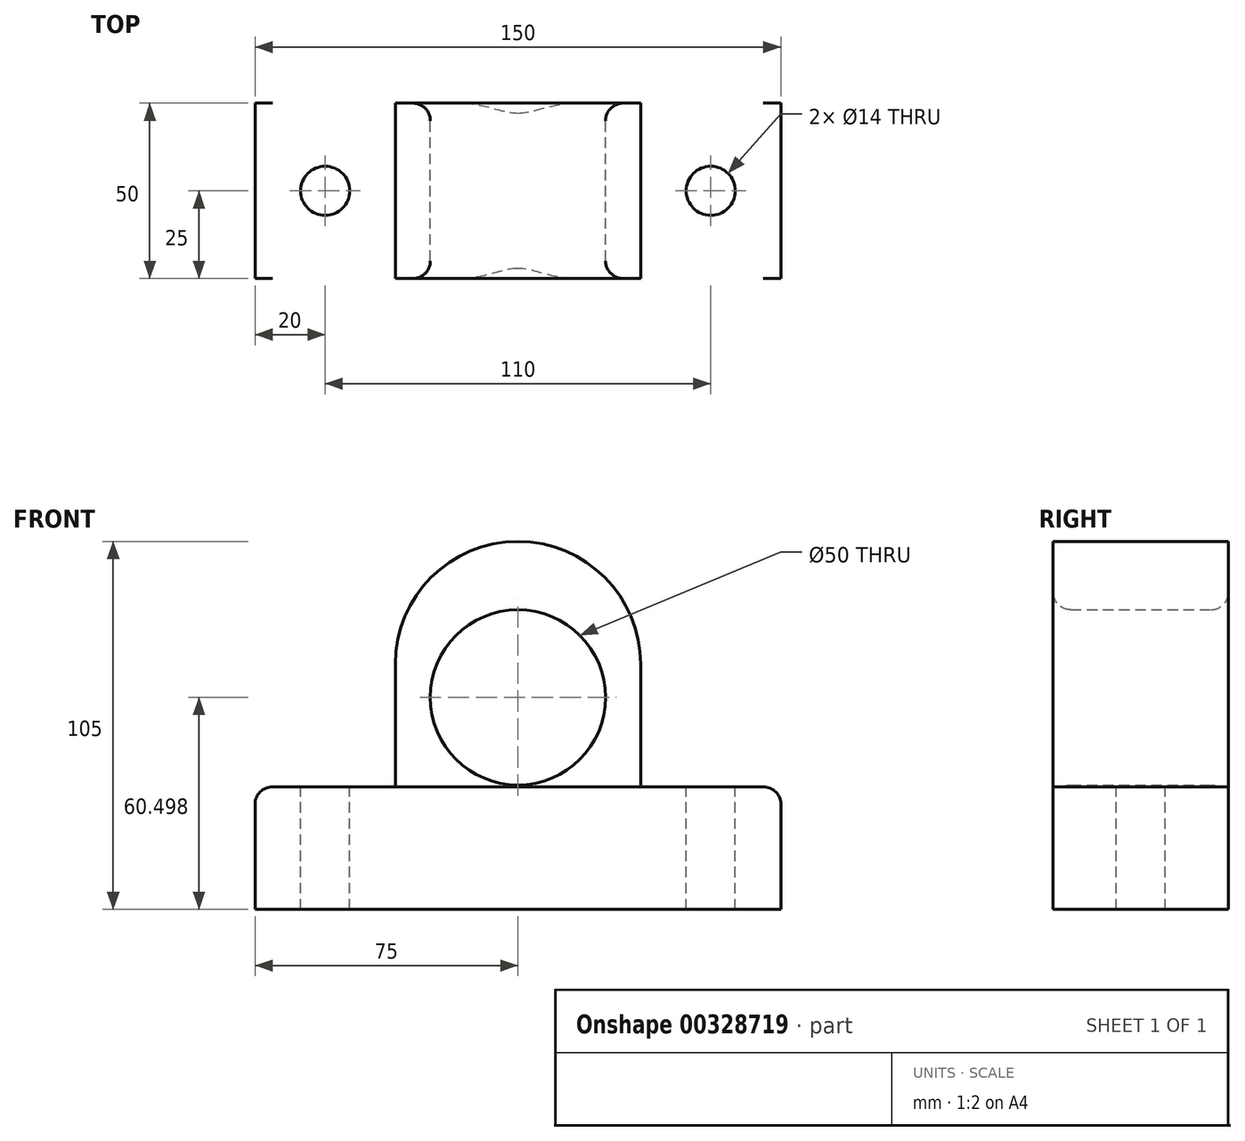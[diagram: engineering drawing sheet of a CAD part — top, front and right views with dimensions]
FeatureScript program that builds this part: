
annotation { "Feature Type Name" : "Feature", "Feature Type Description" : "" }
export const myFeature = defineFeature(function(context is Context, id is Id, definition is map)
    precondition{}
    {
        {
            var Q0;
            Q0=qCreatedBy(makeId("Front.planeOp"),FACE);
            var sketch = newSketch(context, id + "F0", { "sketchPlane" : qUnion([Q0])});
            skLineSegment(sketch, "E0.bottom", {"start": v(75, -17.5) * mm, "end": v(-75, -17.5) * mm});
            skLineSegment(sketch, "E0.top", {"start": v(75, 17.5) * mm, "end": v(-75, 17.5) * mm});
            skLineSegment(sketch, "E0.left", {"start": v(75, -17.5) * mm, "end": v(75, 17.5) * mm});
            skLineSegment(sketch, "E0.right", {"start": v(-75, -17.5) * mm, "end": v(-75, 17.5) * mm});
            skPoint(sketch, "E0.middle", {"position": v(0, 0) * mm});
            skSolve(sketch);
        }
        {
            var Q0;
            Q0=qCreatedBy(makeId("Front.planeOp"),FACE);
            var sketch = newSketch(context, id + "F1", { "sketchPlane" : qUnion([Q0])});
            skLineSegment(sketch, "E1.bottom", {"start": v(-35, 17.5) * mm, "end": v(35, 17.5) * mm});
            skLineSegment(sketch, "E1.top", {"start": v(-35, 87.5) * mm, "end": v(35, 87.5) * mm});
            skLineSegment(sketch, "E1.left", {"start": v(-35, 17.5) * mm, "end": v(-35, 87.5) * mm});
            skLineSegment(sketch, "E1.right", {"start": v(35, 17.5) * mm, "end": v(35, 87.5) * mm});
            skCircle(sketch, "E2", {"center": v(0, 43) * mm, "radius": 25 * mm});
            skSolve(sketch);
        }
        {
            var Q0;
            Q0=makeQuery(id+"F0.imprint","IMPRINT",FACE,{"disambiguationData":[TD([[makeQuery(id+"F0.imprint","IMPRINT",EDGE,{"derivedFrom":sQuery(id+"F0.wireOp",EDGE,"E0.bottom")}),-1.0]])]});
            var Q1;
            Q1=makeQuery(id+"F1.imprint","IMPRINT",FACE,{"disambiguationData":[TD([[makeQuery(id+"F1.imprint","IMPRINT",EDGE,{"derivedFrom":sQuery(id+"F1.wireOp",EDGE,"E1.bottom")}),1.0]])]});
            extrude(context, id + "F2", {"entities" : qUnion([Q0, Q1]), "depth" : 50 * mm});
        }
        {
            var Q0;
            Q0=makeQuery(id+"F2.opExtrude","SWEPT_EDGE",EDGE,{"disambiguationData":[OSD([sQuery(id+"F1.wireOp",EDGE,"E1.top"),sQuery(id+"F1.wireOp",EDGE,"E1.right")])]});
            var Q1;
            Q1=makeQuery(id+"F2.opExtrude","SWEPT_EDGE",EDGE,{"disambiguationData":[OSD([sQuery(id+"F1.wireOp",EDGE,"E1.top"),sQuery(id+"F1.wireOp",EDGE,"E1.left")])]});
            fillet(context, id + "F3", {"entities" : qUnion([Q0, Q1]), "radius" : 35 * mm, "tangentPropagation" : true, "allowEdgeOverflow" : false});
        }
        {
            var Q0;
            Q0=makeQuery(id+"F2.opExtrude","CAP_EDGE",EDGE,{"disambiguationData":[OSD([sQuery(id+"F1.wireOp",EDGE,"E2")])],"isStart":true});
            var Q1;
            {var subQ0=sQuery(id+"F1.wireOp",EDGE,"E1.right");var subQ1=sQuery(id+"F1.wireOp",EDGE,"E1.top");Q1=makeQuery(id+"F3.opFillet","BLEND_EDGE",EDGE,{"blendedFrom":[makeQuery(id+"F2.opExtrude","SWEPT_EDGE",EDGE,{"disambiguationData":[OSD([subQ1,subQ0])]}),makeQuery(id+"F2.opExtrude","CAP_FACE",FACE,{"disambiguationData":[OSD([sQuery(id+"F1.wireOp",EDGE,"E1.bottom"),subQ1,sQuery(id+"F1.wireOp",EDGE,"E1.left"),subQ0,sQuery(id+"F1.wireOp",EDGE,"E2")])],"isStart":true})],"blendedInto":[makeQuery(id+"F2.opExtrude","CAP_FACE",FACE,{"disambiguationData":[OSD([sQuery(id+"F1.wireOp",EDGE,"E1.bottom"),subQ1,sQuery(id+"F1.wireOp",EDGE,"E1.left"),subQ0,sQuery(id+"F1.wireOp",EDGE,"E2")])],"isStart":true})]});}
            fillet(context, id + "F4", {"entities" : qUnion([Q0, Q1]), "radius" : 5 * mm, "tangentPropagation" : true, "allowEdgeOverflow" : false});
        }
        {
            var Q0;
            Q0=makeQuery(id+"F2.opExtrude","SWEPT_FACE",FACE,{"disambiguationData":[OSD([sQuery(id+"F0.wireOp",EDGE,"E0.top")])]});
            var sketch = newSketch(context, id + "F5", { "sketchPlane" : qUnion([Q0])});
            skCircle(sketch, "E3", {"center": v(-55, -25) * mm, "radius": 8 * mm});
            skCircle(sketch, "E4", {"center": v(55, -25) * mm, "radius": 8 * mm});
            skSolve(sketch);
        }
        {
            var Q0;
            Q0=sQuery(id+"F5.wireOp",VERTEX,"E3.center");
            var Q1;
            Q1=sQuery(id+"F5.wireOp",VERTEX,"E4.center");
            var Q2;
            Q2=makeQuery(id+"F2.opExtrude","SWEPT_BODY",BODY,{"disambiguationData":[OSD([sQuery(id+"F0.wireOp",EDGE,"E0.bottom"),sQuery(id+"F0.wireOp",EDGE,"E0.top"),sQuery(id+"F0.wireOp",EDGE,"E0.left"),sQuery(id+"F0.wireOp",EDGE,"E0.right")])]});
            hole(context, id + "F6", {"style" : HoleStyle.SIMPLE, "endStyle" : HoleEndStyle.THROUGH, "standardTappedOrClearance" : lookupTablePath({ "standard" : "ISO", "engagement" : "75%", "pitch" : "2 mm", "size" : "M16", "type" : "Tapped" }), "standardBlindInLast" : lookupTablePath({ "standard" : "ISO", "engagement" : "75%", "pitch" : "2 mm", "size" : "M16", "type" : "Tapped" }), "holeDiameter" : 14 * mm, "showTappedDepth" : true, "tappedDepth" : 12 * mm, "tapClearance" : 3, "locations" : qUnion([Q0, Q1]), "scope" : qUnion([Q2]), "majorDiameter" : 16 * mm});
        }
        {
            var Q0;
            Q0=makeQuery(id+"F2.opExtrude","CAP_EDGE",EDGE,{"disambiguationData":[OSD([sQuery(id+"F1.wireOp",EDGE,"E2")])],"isStart":false});
            var Q1;
            Q1=makeQuery(id+"F2.opExtrude","SWEPT_EDGE",EDGE,{"disambiguationData":[OSD([sQuery(id+"F0.wireOp",EDGE,"E0.top"),sQuery(id+"F0.wireOp",EDGE,"E0.left")])]});
            var Q2;
            Q2=makeQuery(id+"F2.opExtrude","SWEPT_EDGE",EDGE,{"disambiguationData":[OSD([sQuery(id+"F0.wireOp",EDGE,"E0.top"),sQuery(id+"F0.wireOp",EDGE,"E0.right")])]});
            fillet(context, id + "F7", {"entities" : qUnion([Q0, Q1, Q2]), "radius" : 5 * mm, "tangentPropagation" : true, "allowEdgeOverflow" : false});
        }
    });
